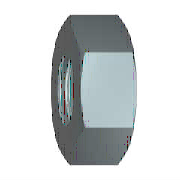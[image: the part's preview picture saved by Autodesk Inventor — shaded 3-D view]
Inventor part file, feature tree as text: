
AUTODESK INVENTOR PART (.ipt)
format: ipt  version: 2015 (Build 190159000, 159)  size: 161,792 bytes
history: native  units: mm (DEFAULTED — no unit token found)
features: sketch x3, chamfer x1, hole x1, other x1, plane x1
ambient origin geometry x7: Origin, YZ Plane, XZ Plane, X Axis, Y Axis, Z Axis, Center Point
bodies: Solid1 (feature_tree), Body (feature_tree)
feature tree (7):
  chamfer  "Chamfer1"  Angle=30.0deg  [1 undecoded]
  hole  "Thread"  [1 undecoded]
  other  "Work Axis1"
  plane  "Work Plane1"
  sketch  "Sketch1"  dims[d0=19.629909mm]
  sketch  "Sketch2"  dims[d1=8.0mm]
  sketch  "Sketch3"  dims[d2=0.0mm d3=30.0deg d4=30.0deg d5=15.3mm d6=15.3mm d7=90.0deg d25=8.647mm d26=6.0mm d27=4.0mm d28=2.0mm d29=14.3117mm d30=8.0mm d31=20.594885mm d8=0.676582mm d9=30.0deg d10=0.676582mm d11=30.0deg d13=0.0mm d14=0.0mm d39=0.0mm d40=0.676582mm d41=0.676582mm d42=0.0mm]
note: 2 required parameter values undecoded (feature->parameter linkage not recoverable at this tier; creation-order binding heuristic only, values carry confidence <= 0.55)
